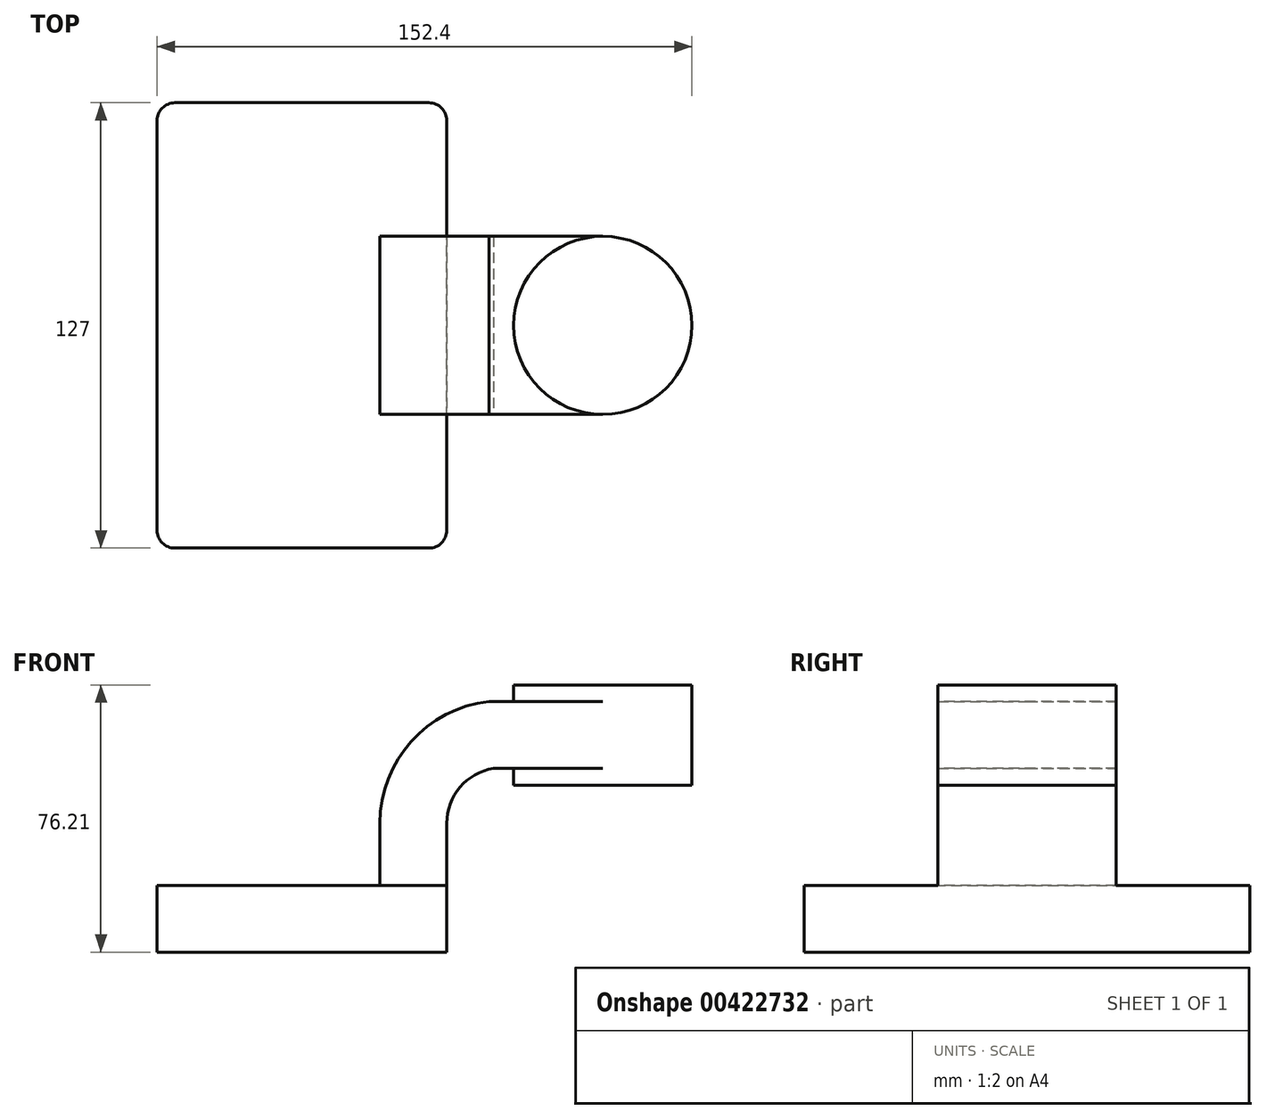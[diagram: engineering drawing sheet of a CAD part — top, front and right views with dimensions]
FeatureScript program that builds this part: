
annotation { "Feature Type Name" : "Feature", "Feature Type Description" : "" }
export const myFeature = defineFeature(function(context is Context, id is Id, definition is map)
    precondition{}
    {
        {
            var Q0;
            Q0=qCreatedBy(makeId("Front.planeOp"),FACE);
            var sketch = newSketch(context, id + "F0", { "sketchPlane" : qUnion([Q0])});
            skLineSegment(sketch, "E0.bottom", {"start": v(41.27, 9.53) * mm, "end": v(-41.28, 9.53) * mm});
            skLineSegment(sketch, "E0.top", {"start": v(41.28, -9.52) * mm, "end": v(-41.27, -9.52) * mm});
            skLineSegment(sketch, "E0.left", {"start": v(41.28, 9.53) * mm, "end": v(41.28, -9.52) * mm});
            skLineSegment(sketch, "E0.right", {"start": v(-41.28, 9.53) * mm, "end": v(-41.27, -9.52) * mm});
            skPoint(sketch, "E0.middle", {"position": v(0, 0) * mm});
            skLineSegment(sketch, "E1.bottom", {"start": v(111.12, 66.68) * mm, "end": v(60.33, 66.68) * mm});
            skLineSegment(sketch, "E1.top", {"start": v(111.13, 38.1) * mm, "end": v(60.33, 38.1) * mm});
            skLineSegment(sketch, "E1.left", {"start": v(111.12, 66.68) * mm, "end": v(111.13, 38.1) * mm});
            skLineSegment(sketch, "E1.right", {"start": v(60.33, 66.68) * mm, "end": v(60.33, 38.1) * mm});
            skPoint(sketch, "E1.middle", {"position": v(85.73, 52.39) * mm});
            skLineSegment(sketch, "E2", {"start": v(41.27, 9.53) * mm, "end": v(41.27, 27.21) * mm});
            skArc(sketch, "E3", {"start": v(41.27, 27.21) * mm, "mid": v(45.05, 37.48) * mm, "end": v(54.56, 42.88) * mm});
            skLineSegment(sketch, "E4", {"start": v(54.56, 42.88) * mm, "end": v(85.73, 42.88) * mm});
            skLineSegment(sketch, "E5.0", {"start": v(53.3, 61.93) * mm, "end": v(85.73, 61.93) * mm});
            skArc(sketch, "E5.1", {"start": v(22.22, 27.21) * mm, "mid": v(31.13, 50.51) * mm, "end": v(53.3, 61.93) * mm});
            skLineSegment(sketch, "E5.2", {"start": v(22.22, 9.53) * mm, "end": v(22.22, 27.21) * mm});
            skLineSegment(sketch, "E6", {"start": v(85.73, 38.1) * mm, "end": v(85.73, 66.68) * mm});
            skFitSpline(sketch, "E7", {"points": [v(-41.28, 9.53) * mm, v(53.3, 61.93) * mm], "startDerivative": vector(1.7, 124.37) * mm, "endDerivative": vector(141.66, 2) * mm});
            skSolve(sketch);
        }
        {
            var Q0;
            Q0=makeQuery(id+"F0.imprint","IMPRINT",FACE,{"disambiguationData":[TD([[makeQuery(id+"F0.imprint","IMPRINT",EDGE,{"derivedFrom":sQuery(id+"F0.wireOp",EDGE,"E0.top")}),-1.0]])]});
            extrude(context, id + "F1", {"entities" : qUnion([Q0]), "endBound" : BoundingType.SYMMETRIC, "depth" : 127 * mm});
        }
        {
            var Q0;
            {var subQ1=sQuery(id+"F0.wireOp",EDGE,"E2");Q0=makeQuery(id+"F0.imprint","IMPRINT",FACE,{"disambiguationData":[TD([[makeQuery(id+"F0.imprint","IMPRINT",EDGE,{"derivedFrom":subQ1}),1.0]])]});}
            var Q1;
            {var subQ0=sQuery(id+"F0.wireOp",EDGE,"E5.0");var subQ1=sQuery(id+"F0.wireOp",EDGE,"E1.right");var subQ2=makeQuery(id+"F0.imprint","INTERSECT",VERTEX,{"derivedFrom":[subQ1,subQ0]});Q1=makeQuery(id+"F0.imprint","IMPRINT",FACE,{"disambiguationData":[TD([[makeQuery(id+"F0.imprint","IMPRINT",EDGE,{"disambiguationData":[TD([[subQ2,-1.0]])],"derivedFrom":subQ1}),1.0]])]});}
            extrude(context, id + "F2", {"entities" : qUnion([Q0, Q1]), "operationType" : NewBodyOperationType.ADD, "endBound" : BoundingType.SYMMETRIC, "oppositeDirection" : true, "depth" : 50.8 * mm});
        }
        {
            var Q0;
            Q0=makeQuery(id+"F0.imprint","IMPRINT",FACE,{"disambiguationData":[TD([[makeQuery(id+"F0.imprint","IMPRINT",EDGE,{"derivedFrom":sQuery(id+"F0.wireOp",EDGE,"E5.1")}),1.0]])]});
            extrude(context, id + "F3", {"entities" : qUnion([Q0]), "operationType" : NewBodyOperationType.ADD, "endBound" : BoundingType.SYMMETRIC, "depth" : 15.88 * mm});
        }
        {
            var Q0;
            {var subQ4=sQuery(id+"F0.wireOp",EDGE,"E1.left");Q0=makeQuery(id+"F0.imprint","IMPRINT",FACE,{"disambiguationData":[TD([[makeQuery(id+"F0.imprint","IMPRINT",EDGE,{"derivedFrom":subQ4}),-1.0]])]});}
            var Q1;
            Q1=sQuery(id+"F0.wireOp",EDGE,"E6");
            revolve(context, id + "F4", {"operationType" : NewBodyOperationType.ADD, "entities" : qUnion([Q0]), "axis" : qUnion([Q1]), "revolveType" : RevolveType.FULL});
        }
        {
            var Q0;
            Q0=makeQuery(id+"F1.opExtrude","CAP_EDGE",EDGE,{"disambiguationData":[OSD([sQuery(id+"F0.wireOp",EDGE,"E0.left")])],"isStart":false});
            fillet(context, id + "F5", {"entities" : qUnion([Q0]), "radius" : 5.08 * mm, "tangentPropagation" : true, "allowEdgeOverflow" : false});
        }
        {
            var Q0;
            Q0=makeQuery(id+"F1.opExtrude","CAP_EDGE",EDGE,{"disambiguationData":[OSD([sQuery(id+"F0.wireOp",EDGE,"E0.left")])],"isStart":true});
            fillet(context, id + "F6", {"entities" : qUnion([Q0]), "radius" : 5.08 * mm, "tangentPropagation" : true, "allowEdgeOverflow" : false});
        }
        {
            var Q0;
            Q0=makeQuery(id+"F1.opExtrude","CAP_EDGE",EDGE,{"disambiguationData":[OSD([sQuery(id+"F0.wireOp",EDGE,"E0.right")])],"isStart":true});
            fillet(context, id + "F7", {"entities" : qUnion([Q0]), "radius" : 5.08 * mm, "tangentPropagation" : true, "allowEdgeOverflow" : false});
        }
        {
            var Q0;
            Q0=makeQuery(id+"F1.opExtrude","CAP_EDGE",EDGE,{"disambiguationData":[OSD([sQuery(id+"F0.wireOp",EDGE,"E0.right")])],"isStart":false});
            fillet(context, id + "F8", {"entities" : qUnion([Q0]), "radius" : 5.08 * mm, "tangentPropagation" : true, "allowEdgeOverflow" : false});
        }
    });
